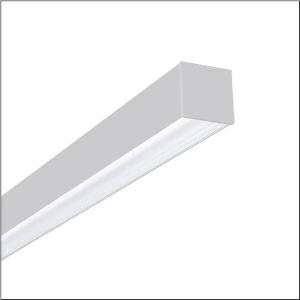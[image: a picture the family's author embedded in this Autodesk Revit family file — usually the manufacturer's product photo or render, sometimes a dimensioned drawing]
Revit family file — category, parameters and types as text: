
# Revit family: silica_r_5mx31bd1w4a_74d2
name_source: partatom
category: Lighting Fixtures
units: mm (PartAtom-declared; Revit-internal decimal feet)

## family parameters
Cut with Voids When Loaded = No
Host = Face
Light Source = No
Part Type = Normal
Room Calculation Point = No
Round Connector Dimension = Use Diameter
Shared = No

## types (1)
- --- (1 x LED, 7070 lm, 45.6 W, 4000K)
    Apparent Load = 46 VA
    CIE Flux Codes = 82 97 100 70 100
    Color Rendering = 80
    Color Temperature = 4000K
    Default Elevation = 1800 mm
    Description = Silica®, office luminaire, of aluminium, light emission: direct/indirect distribution, primary light characteristic: symmetric, installation type: suspended mounting, LED, rated luminous flux: 7.070lm, luminous efficacy: 155lm/W, light colour: 840, colour temperature: 4000K, control gear: ECG DALI, with terminal, 3+2-pole, max. 2.5mm², mains connection: 230V, AC, 50/60Hz, connection cable inclusive, cable length: 1,5m, rated input power: 46W, luminaire housing, of aluminium, traffic white (RAL 9016), length: 1.442mm, width: 65mm, height: 64mm, protection rating (complete): IP20, insulation class (complete): insulation class I (protective earthing), certification: CE, permissible operating ambient temperature: 0..+35°C, standard: EN 50419, packaging unit: 1 piece
    Height = 64 mm
    Lamp = 1 x LED
    Lamp Light Flux = 7070 lm
    Lamp Power = 45.6 W
    Lamp count = 1
    Length = 1442 mm
    Luminous efficacy = 155 lm/W
    Manufacturer = Siteco
    ModVariant = No
    Model = 5MX31BD1W4A
    Mounting Place = Ceiling
    Mounting Type = Pendant
    Number of Poles = 1
    OnlyDefault = Yes
    Power Factor = 1
    Product Name = Silica®
    Product group = office luminaire | ceiling pendant
    ProductGroupID = 902
    Protection Class = Protection class I
    Protection Degree = IP 20
    RLX_Detail_Level = 1
    RLX_Emergency_Light_Flux = 0 lm
    RLX_Emergency_Type = 0
    RLX_Emergency_Type_DB = No
    RlxData = <blob elided: 28953 chars, md5=6e96e357>
    Socket = socket
    Standby Power = 0 W
    System Light Flux = 7070 lm
    System Power = 46 W
    Type Comments = factory setting: direct and indirect light
    Type Image = l_1003924.jpg
    URL = http://relux.com
    VarID = @adj_138216
    Voltage = 0 V
    Weight = 0.00 kg
    Width = 66 mm

## geometry (parser evidence)
native form markers: Blend x4, Sweep x14
no freeform markers — native parametric forms only
